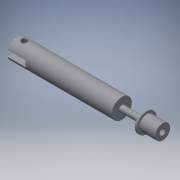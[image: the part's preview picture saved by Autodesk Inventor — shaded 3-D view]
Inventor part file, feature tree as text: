
AUTODESK INVENTOR PART (.ipt)
format: ipt  version: 2017 (Build 210142000, 142)  size: 189,952 bytes
history: native  units: in
note: dims shown in document units (in); Inventor stores cm internally (conversion verified against a paired STEP export)
features: extrude x11, sketch x11
ambient origin geometry x8: Origin, YZ Plane, XZ Plane, XY Plane, X Axis, Y Axis, Z Axis, Center Point
bodies: Solid1 (feature_tree)
feature tree (22):
  extrude  "Extrusion1"  Depth=0.3937in TaperAngle=0.0deg
  extrude  "Extrusion2"  Depth=0.4528in TaperAngle=0.0deg
  extrude  "Extrusion3"  Depth=0.3937in TaperAngle=0.0deg
  extrude  "Extrusion4"  Depth=0.315in TaperAngle=0.0deg
  extrude  "Extrusion5"  Depth=0.315in TaperAngle=0.0deg
  extrude  "Extrusion6"  Depth=0.3937in
  extrude  "Extrusion7"  Depth=0.6693in
  extrude  "Extrusion8"  Depth=0.4724in
  extrude  "Extrusion10"  Depth=0.374in TaperAngle=0.0deg
  extrude  "Extrusion12"  Depth=0.3543in TaperAngle=0.0deg
  extrude  "Extrusion13"  Depth=0.3937in
  sketch  "Sketch1"  dims[d0=0.3937in d1=2.0669in d2=0.0in]
  sketch  "Sketch2"  dims[d3=0.1181in d4=0.4528in d5=0.0in]
  sketch  "Sketch3"  dims[d6=0.3937in d7=0.0394in d8=0.0in]
  sketch  "Sketch4"  dims[d9=0.2953in d10=0.315in d11=0.0in]
  sketch  "Sketch5"  dims[d12=0.1181in d13=0.315in d14=0.0in]
  sketch  "Sketch6"  dims[d15=0.3543in d16=0.3937in]
  sketch  "Sketch7"  dims[d17=0.4134in d18=0.0in d19=0.6693in]
  sketch  "Sketch8"  dims[d20=0.0394in d21=0.0in d23=0.4724in]
  sketch  "Sketch10"  dims[d24=0.3543in d25=0.0in d31=0.374in d32=0.0in]
  sketch  "Sketch12"  dims[d35=0.1181in d36=0.3543in d37=0.0in]
  sketch  "Sketch13"  dims[d38=0.2756in d39=0.1181in d40=0.3937in d41=0.0in]
